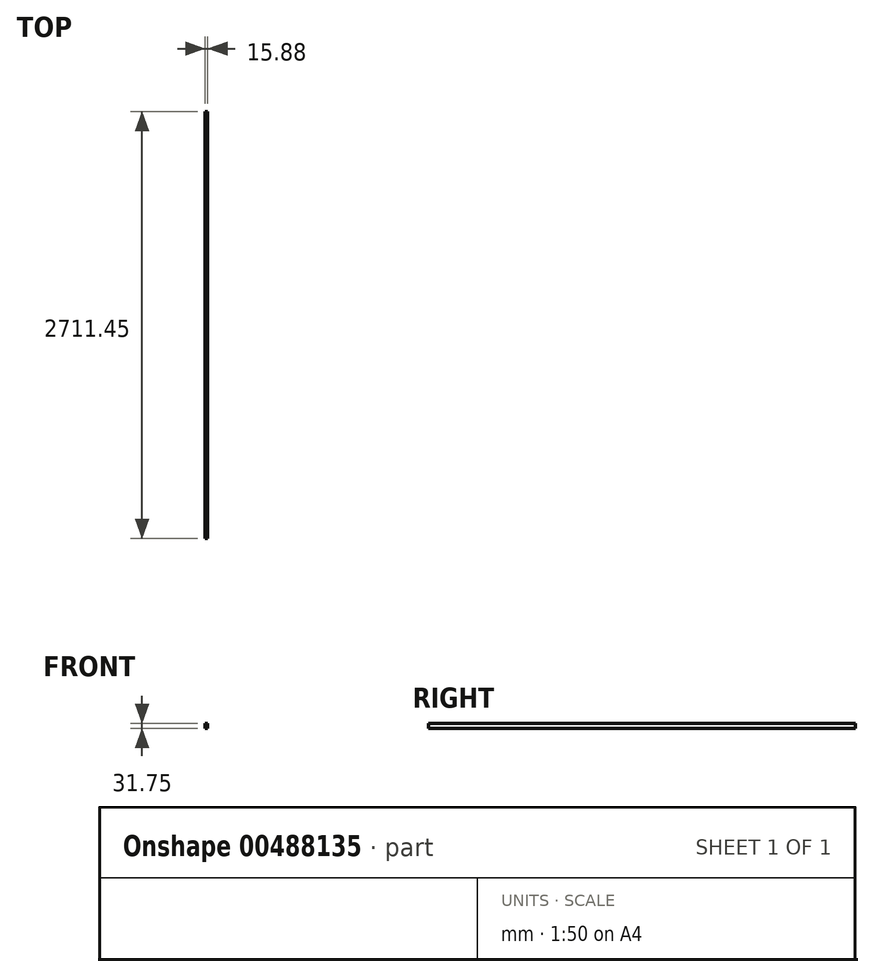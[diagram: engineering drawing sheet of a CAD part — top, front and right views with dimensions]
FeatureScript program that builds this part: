
annotation { "Feature Type Name" : "Feature", "Feature Type Description" : "" }
export const myFeature = defineFeature(function(context is Context, id is Id, definition is map)
    precondition{}
    {
        {
            var Q0;
            Q0=qCreatedBy(makeId("Front.planeOp"),FACE);
            var sketch = newSketch(context, id + "F0", { "sketchPlane" : qUnion([Q0])});
            skLineSegment(sketch, "E0", {"start": v(0, 0) * mm, "end": v(15.88, 0) * mm});
            skLineSegment(sketch, "E1", {"start": v(0, 0) * mm, "end": v(0, -31.75) * mm});
            skLineSegment(sketch, "E2", {"start": v(0, -31.75) * mm, "end": v(15.88, -31.75) * mm});
            skLineSegment(sketch, "E3", {"start": v(15.88, -31.75) * mm, "end": v(15.88, 0) * mm});
            skSolve(sketch);
        }
        {
            var Q0;
            Q0=makeQuery(id+"F0.imprint","IMPRINT",FACE,{"disambiguationData":[TD([[makeQuery(id+"F0.imprint","IMPRINT",EDGE,{"derivedFrom":sQuery(id+"F0.wireOp",EDGE,"E0")}),-1.0]])]});
            var Q1;
            Q1=makeQuery(id+"F0.imprint","IMPRINT",FACE,{"disambiguationData":[TD([[makeQuery(id+"F0.imprint","IMPRINT",EDGE,{"derivedFrom":sQuery(id+"F0.wireOp",EDGE,"E0")}),-1.0]])]});
            var Q2;
            Q2=makeQuery(id+"F0.imprint","IMPRINT",FACE,{"disambiguationData":[TD([[makeQuery(id+"F0.imprint","IMPRINT",EDGE,{"derivedFrom":sQuery(id+"F0.wireOp",EDGE,"sE00Gzr5-o4TN-UCdV-R85f-zcs0Y7AX2MqQ")}),1.0]])]});
            extrude(context, id + "F1", {"entities" : qUnion([Q0, Q1, Q2]), "depth" : 25.4 * mm, "offsetDistance" : 25.4 * mm});
        }
        {
            var Q0;
            Q0=makeQuery(id+"F1.opExtrude","CAP_FACE",FACE,{"disambiguationData":[OSD([sQuery(id+"F0.wireOp",EDGE,"E0"),sQuery(id+"F0.wireOp",EDGE,"E1"),sQuery(id+"F0.wireOp",EDGE,"E2"),sQuery(id+"F0.wireOp",EDGE,"E3")])],"isStart":true});
            extrude(context, id + "F2", {"entities" : qUnion([Q0]), "operationType" : NewBodyOperationType.ADD, "depth" : 2686.05 * mm, "offsetDistance" : 25.4 * mm});
        }
    });
